# Revit family: BuzziSpace - BuzziMoon
name_source: partatom
category: Lighting Fixtures
units: mm (PartAtom-declared; Revit-internal decimal feet)

## family parameters
Always vertical = Yes
Cut with Voids When Loaded = No
Host = Ceiling
Light Source = Yes
OmniClass Number = 23.80.70.11
OmniClass Title = Luminaries for Internal Lighting
Part Type = Normal
Room Calculation Point = No
Round Connector Dimension = Use Diameter
Shared = No

## types (30) — shared parameters
Color Filter = 16777215
Dimming Lamp Color Temperature Shift = <None>
Light Source Symbol Size = 2' - 0"
Manufacturer = BuzziSpace

## per-type parameters (varying)
| type | Drop L | Drop M | Drop S | Flat L | Flat M | Flat S | Leaf L | Leaf M | Leaf S | Oval | Oval Flat M | Oval Flat S | Oval Leaf M | Oval Leaf S | Oval Rib M | Oval Rib S | Rib L | Rib M | Rib S | Surface Mount | Suspension | Suspension Length | Suspension Visibility |
| 3D Drop L- Suspended | Yes | No | No | No | No | No | No | No | No | No | No | No | No | No | No | No | No | No | No | No | 3' - 0" | 3' - 0" | Yes |
| 3D Drop M- Suspended | No | Yes | No | No | No | No | No | No | No | No | No | No | No | No | No | No | No | No | No | No | 3' - 0" | 3' - 0" | Yes |
| 3D Drop S- Suspended | No | No | Yes | No | No | No | No | No | No | No | No | No | No | No | No | No | No | No | No | No | 3' - 0" | 3' - 0" | Yes |
| 3D Leaf L- Suspended | No | No | No | No | No | No | Yes | No | No | No | No | No | No | No | No | No | No | No | No | No | 6' - 0" | 6' - 0" | Yes |
| 3D Leaf M- Suspended | No | No | No | No | No | No | No | Yes | No | No | No | No | No | No | No | No | No | No | No | No | 3' - 0" | 3' - 0" | Yes |
| 3D Leaf S- Suspended | No | No | No | No | No | No | No | No | Yes | No | No | No | No | No | No | No | No | No | No | No | 3' - 0" | 3' - 0" | Yes |
| 3D Rib L- Suspended | No | No | No | No | No | No | No | No | No | No | No | No | No | No | No | No | Yes | No | No | No | 3' - 0" | 3' - 0" | Yes |
| 3D Rib M- Suspended | No | No | No | No | No | No | No | No | No | No | No | No | No | No | No | No | No | Yes | No | No | 3' - 0" | 3' - 0" | Yes |
| 3D Rib S- Suspended | No | No | No | No | No | No | No | No | No | No | No | No | No | No | No | No | No | No | Yes | No | 3' - 0" | 3' - 0" | Yes |
| Flat L- Suspended | No | No | No | Yes | No | No | No | No | No | No | No | No | No | No | No | No | No | No | No | No | 3' - 0" | 3' - 0" | Yes |
| Flat M- Suspended | No | No | No | No | Yes | No | No | No | No | No | No | No | No | No | No | No | No | No | No | No | 3' - 0" | 3' - 0" | Yes |
| Oval 3D Leaf M- Suspended | No | No | No | No | No | No | No | No | No | Yes | Yes | No | Yes | No | No | No | No | No | No | No | 3' - 0" | 3' - 0" | Yes |
| Oval 3D Leaf S- Suspended | No | No | No | No | No | No | No | No | No | Yes | No | No | No | Yes | No | No | No | No | No | No | 3' - 0" | 3' - 0" | Yes |
| Oval 3D Rib M- Suspended | No | No | No | No | No | No | No | No | No | Yes | No | No | No | No | Yes | No | No | No | No | No | 3' - 0" | 3' - 0" | Yes |
| Oval 3D Rib S- Suspended | No | No | No | No | No | No | No | No | No | Yes | No | No | No | No | No | Yes | No | No | No | No | 3' - 0" | 3' - 0" | Yes |
| Oval Flat M- Suspended | No | No | No | No | No | No | No | No | No | Yes | Yes | No | No | No | No | No | No | No | No | No | 3' - 0" | 3' - 0" | Yes |
| Oval Flat S- Suspended | No | No | No | No | No | No | No | No | No | Yes | No | Yes | No | No | No | No | No | No | No | No | 3' - 0" | 3' - 0" | Yes |
| Flat S- Suspended | No | No | No | No | No | Yes | No | No | No | No | No | No | No | No | No | No | No | No | No | No | 3' - 0" | 3' - 0" | Yes |
| 3D Rib L- Ceiling Mounted | No | No | No | No | No | No | No | No | No | No | No | No | No | No | No | No | Yes | No | No | Yes | 0' - 2 3/4" | 6' - 0" | No |
| 3D Rib M- Ceiling Mounted | No | No | No | No | No | No | No | No | No | No | No | No | No | No | No | No | No | Yes | No | Yes | 0' - 2 3/4" | 6' - 0" | No |
| 3D Rib S- Ceiling Mounted | No | No | No | No | No | No | No | No | No | No | No | No | No | No | No | No | No | No | Yes | Yes | 0' - 2 3/4" | 6' - 0" | No |
| 3D Leaf L- Ceiling Mounted | No | No | No | No | No | No | Yes | No | No | No | No | No | No | No | No | No | No | No | No | Yes | 0' - 2 3/4" | 6' - 0" | No |
| 3D Leaf M- Ceiling Mounted | No | No | No | No | No | No | No | Yes | No | No | No | No | No | No | No | No | No | No | No | Yes | 0' - 2 3/4" | 6' - 0" | No |
| 3D Leaf S- Ceiling Mounted | No | No | No | No | No | No | No | No | Yes | No | No | No | No | No | No | No | No | No | No | Yes | 0' - 2 3/4" | 6' - 0" | No |
| 3D Drop L- Ceiling Mounted | Yes | No | No | No | No | No | No | No | No | No | No | No | No | No | No | No | No | No | No | Yes | 0' - 2 3/4" | 6' - 0" | No |
| 3D Drop M- Ceiling Mounted | No | Yes | No | No | No | No | No | No | No | No | No | No | No | No | No | No | No | No | No | Yes | 0' - 2 3/4" | 6' - 0" | No |
| 3D Drop S- Ceiling Mounted | No | No | Yes | No | No | No | No | No | No | No | No | No | No | No | No | No | No | No | No | Yes | 0' - 2 3/4" | 6' - 0" | No |
| Flat L- Ceiling Mounted | No | No | No | Yes | No | No | No | No | No | No | No | No | No | No | No | No | No | No | No | Yes | 0' - 2 3/4" | 6' - 0" | No |
| Flat M- Ceiling Mounted | No | No | No | No | Yes | No | No | No | No | No | No | No | No | No | No | No | No | No | No | Yes | 0' - 2 3/4" | 6' - 0" | No |
| Flat S- Ceiling Mounted | No | No | No | No | No | Yes | No | No | No | No | No | No | No | No | No | No | No | No | No | Yes | 0' - 2 3/4" | 6' - 0" | No |

## geometry (parser evidence)
native form markers: Sweep x7
no freeform markers — native parametric forms only
